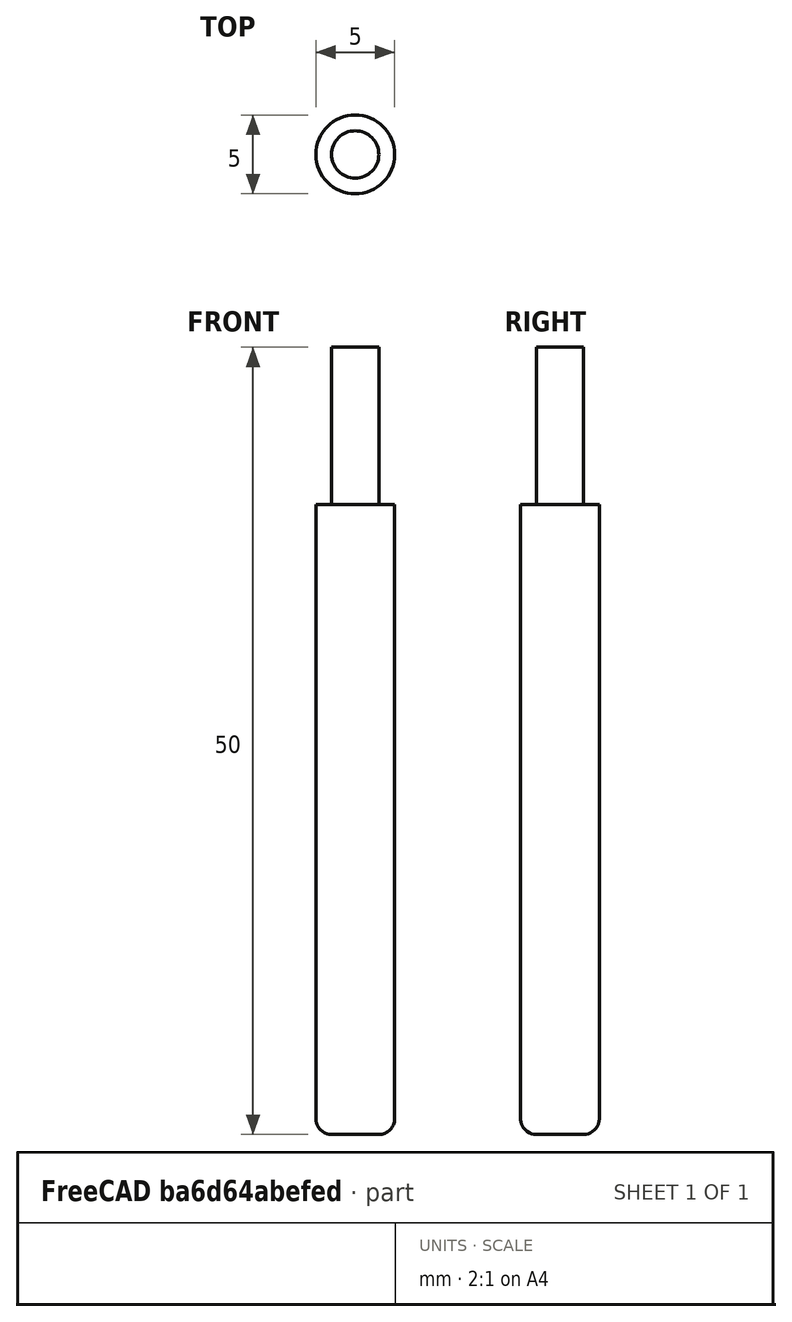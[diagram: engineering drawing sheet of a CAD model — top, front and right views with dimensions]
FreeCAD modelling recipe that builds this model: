
FCSTD DOCUMENT  (FreeCAD 0.19R24049 (Git))
Label: bullnose
License: All rights reserved
LicenseURL: http://en.wikipedia.org/wiki/All_rights_reserved
objects: Sketcher::SketchObject×1, PartDesign::Revolution×1, App::FeaturePython×1, PartDesign::Body×1
note: 4 computed .brp shape members not serialized (recipe doc carries the construction recipe); baked Part::Feature solids carry a one-line shape summary decoded from their .brp

FEATURE [Sketcher::SketchObject] Sketch
  FullyConstrained = true
  MapMode = 5
  Placement = pos=(0,0,0) rot=(1,0,0;1.5708rad)
  Support = -> [XZ_Plane]
  expr: Constraints[12] = <<Attributes>>.ShankDiameter
  expr: Constraints[6] = <<Attributes>>.Length
  expr: Constraints[20] = <<Attributes>>.CuttingEdgeHeight
  expr: Constraints[5] = <<Attributes>>.Diameter
  expr: Constraints[19] = <<Attributes>>.FlatRadius
  sketch-geometry (9):
    g0: LineSegment StartX=0 StartY=50 StartZ=0 EndX=0 EndY=0 EndZ=0
    g1: LineSegment StartX=0 StartY=0 StartZ=0 EndX=1.5 EndY=0 EndZ=0
    g2: LineSegment StartX=2.5 StartY=1 StartZ=0 EndX=2.5 EndY=40 EndZ=0
    g3: LineSegment StartX=1.5 StartY=50 StartZ=0 EndX=0 EndY=50 EndZ=0
    g4: LineSegment StartX=2.5 StartY=0 StartZ=0 EndX=-2.5 EndY=0 EndZ=0
    g5: LineSegment StartX=1.5 StartY=40.01 StartZ=0 EndX=2.5 EndY=40 EndZ=0
    g6: LineSegment StartX=1.5 StartY=50 StartZ=0 EndX=1.5 EndY=40.01 EndZ=0
    g7: LineSegment StartX=-1.5 StartY=50 StartZ=0 EndX=1.5 EndY=50 EndZ=0
    g8: ArcOfCircle CenterX=1.5 CenterY=1 CenterZ=0 NormalX=0 NormalY=0 NormalZ=1 AngleXU=0 Radius=1 StartAngle=4.71239 EndAngle=6.28319
  constraints (24):
    c: Vertical(g0)
    c: Coincident(g0,g1)
    c: Horizontal(g1)
    c: Vertical(g2)
    c: Horizontal(g3)
    c: DistanceX(g4,g4) = 5
    c: DistanceY(g4,g3) = 50
    c: Coincident(g2,g5)
    c: Vertical(g6)
    c: Coincident(g3,g6)
    c: Symmetric(g7,g7,g0)
    c: Coincident(g7,g3)
    c: DistanceX(g7,g7) = 3
    c: Coincident(g5,g6)
    c: Tangent(g1,g8) = -1.5708
    c: Tangent(g2,g8) = -1.5708
    c: PointOnObject(g0,g4)
    c: Symmetric(g4,g4,g-2)
    c: Vertical(g4,g2)
    c: DistanceX(g1,g1) = 1.5
    c: DistanceY(g1,g2) = 40
    c: Coincident(g0,g3)
    c: Coincident(g-1,g0)
    c: DistanceY(g2,g5) = 0.01
FEATURE [PartDesign::Revolution] Revolution
  AllowMultiFace = false
  Angle = 360
  Axis = (0,-2e-16,1)
  Base = (0,0,0)
  Placement = pos=(0,0,0) rot=(1,0,0;1.5708rad)
  Profile = -> Sketch
  ReferenceAxis = -> Sketch [V_Axis]
  Reversed = true
FEATURE [App::FeaturePython] PropertyBag  label="Attributes"  # WARN: FeaturePython — macro-defined, semantics opaque (R4)
  Chipload = 0
  CustomPropertyGroups = Attributes | Shape
  CuttingEdgeHeight = 40
  Diameter = 5
  FlatRadius = 1.5
  Flutes = 0
  Length = 50
  Material = 0
  ShankDiameter = 3
FEATURE [PartDesign::Body] Body  label="Bullnose"
  Group = -> [Sketch,Revolution,PropertyBag]
  Origin = -> Origin
  Tip = -> Revolution
